# Revit family: BUILDMAT-SNGM020-Maya-380-Gunmetal
name_source: partatom
category: Plumbing Fixtures
units: mm (PartAtom-declared; Revit-internal decimal feet)

## family parameters
Cut with Voids When Loaded = No
Host = Face
Part Type = Normal
Room Calculation Point = No
Round Connector Dimension = Use Diameter
Shared = No

## types (1)
- Maya 380x450x250mm
    Default Elevation = 1219.2 mm  [stored 4 ft]
    Depth = 250 mm  [stored 0.82021 ft]
    Description = BUILDMAT - Maya 380x450 Single Bowl Sink
    Length = 400 mm  [stored 1.31234 ft]
    Manufacturer = BUILDMAT
    Manufacturer URL = https://www.buildmat.com.au
    Material = BUILDMAT Gunmetal
    Middle Bracket = No
    Middle Sound Pad = Yes
    Model = SNA00020
    Side Brackets = Yes
    Side Sound Pad = No
    URL = https://www.buildmat.com.au
    Width = 330 mm

note: [stored X ft] marks values corroborated as IEEE doubles in the binary element streams (Revit-internal decimal feet)

## geometry (parser evidence)
native form markers: Sweep x6
no freeform markers — native parametric forms only
